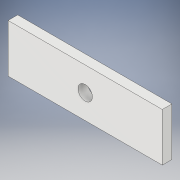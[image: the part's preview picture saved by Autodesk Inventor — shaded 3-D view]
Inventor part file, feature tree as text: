
AUTODESK INVENTOR PART (.ipt)
format: ipt  version: 2017 SP1 (Build 210196100, 196)  size: 97,280 bytes
history: native  units: in
note: dims shown in document units (in); Inventor stores cm internally (conversion verified against a paired STEP export)
features: extrude x2, sketch x2
ambient origin geometry x8: Origin, YZ Plane, XZ Plane, XY Plane, X Axis, Y Axis, Z Axis, Center Point
bodies: Solid1 (feature_tree)
feature tree (4):
  extrude  "Extrusion1"  Depth=0.3937in
  extrude  "Extrusion2"  Depth=0.0787in
  sketch  "Sketch1"  dims[d0=1.2598in d1=0.3937in]
  sketch  "Sketch2"  dims[d2=0.0787in d3=0.0in d4=0.1181in d5=0.0787in d6=0.0in]
